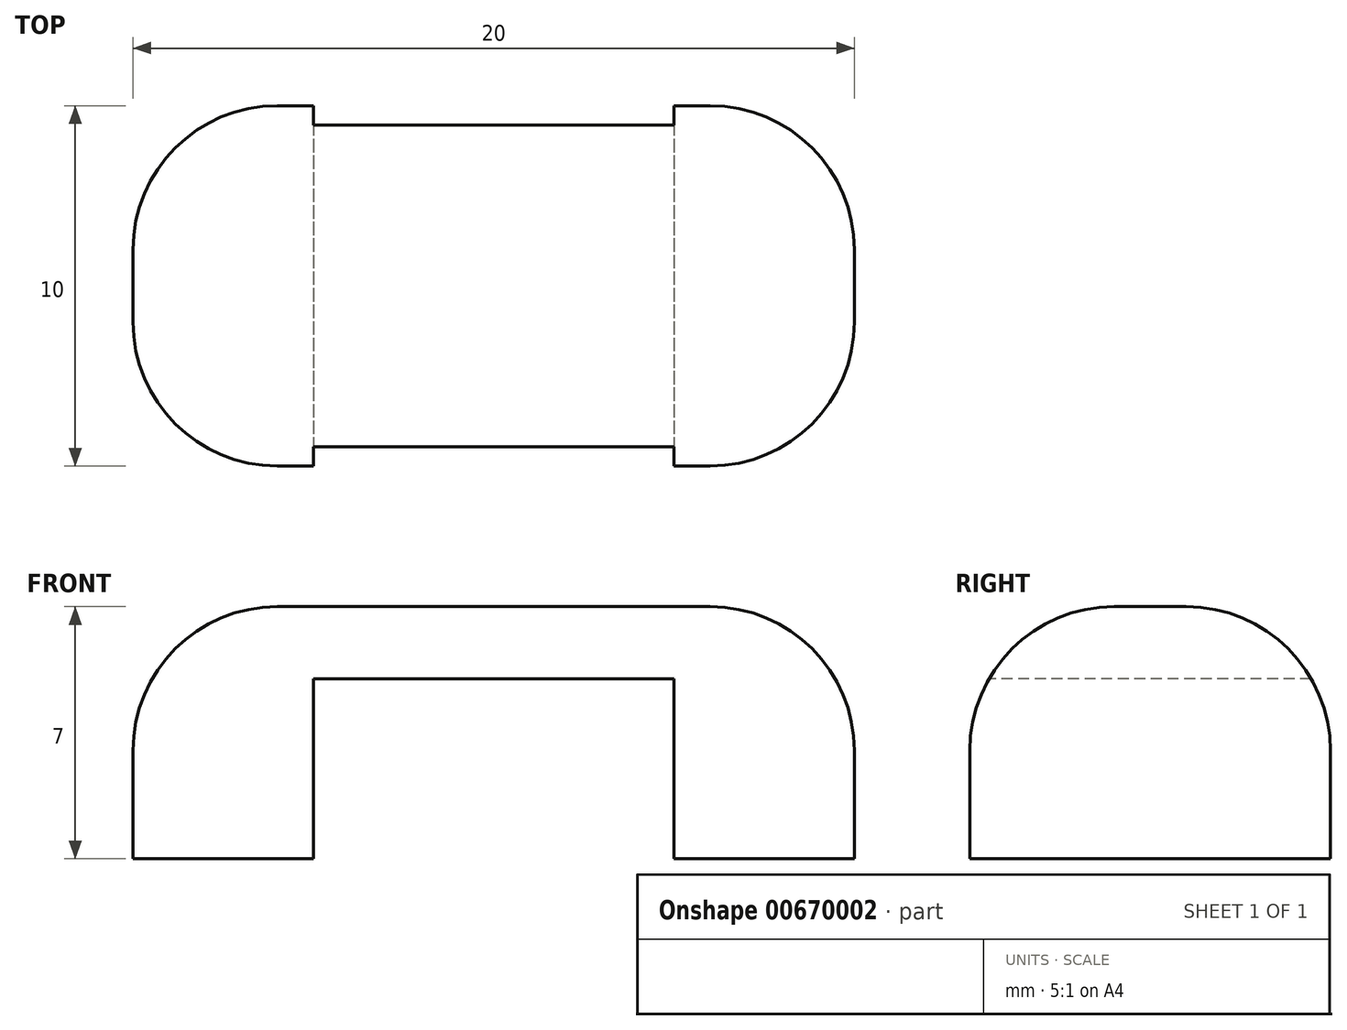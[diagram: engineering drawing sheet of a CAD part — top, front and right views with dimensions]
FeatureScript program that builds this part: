
annotation { "Feature Type Name" : "Feature", "Feature Type Description" : "" }
export const myFeature = defineFeature(function(context is Context, id is Id, definition is map)
    precondition{}
    {
        {
            var Q0;
            Q0=qCreatedBy(makeId("Top.planeOp"),FACE);
            var sketch = newSketch(context, id + "F0", { "sketchPlane" : qUnion([Q0])});
            skLineSegment(sketch, "E0.bottom", {"start": v(-10, 5) * mm, "end": v(-5, 5) * mm});
            skLineSegment(sketch, "E0.top", {"start": v(-10, -5) * mm, "end": v(-5, -5) * mm});
            skLineSegment(sketch, "E0.left", {"start": v(-10, 5) * mm, "end": v(-10, -5) * mm});
            skLineSegment(sketch, "E0.right", {"start": v(-5, 5) * mm, "end": v(-5, -5) * mm});
            skLineSegment(sketch, "E1.bottom", {"start": v(5, 5) * mm, "end": v(10, 5) * mm});
            skLineSegment(sketch, "E1.top", {"start": v(5, -5) * mm, "end": v(10, -5) * mm});
            skLineSegment(sketch, "E1.left", {"start": v(5, 5) * mm, "end": v(5, -5) * mm});
            skLineSegment(sketch, "E1.right", {"start": v(10, 5) * mm, "end": v(10, -5) * mm});
            skSolve(sketch);
        }
        {
            var Q0;
            Q0 = qSketchRegion(id + "F0", true);
            extrude(context, id + "F1", {"entities" : qUnion([Q0]), "depth" : 5 * mm, "offsetDistance" : 25 * mm});
        }
        {
            var Q0;
            Q0=makeQuery(id+"F1.opExtrude","CAP_FACE",FACE,{"disambiguationData":[OSD([sQuery(id+"F0.wireOp",EDGE,"E0.bottom"),sQuery(id+"F0.wireOp",EDGE,"E0.top"),sQuery(id+"F0.wireOp",EDGE,"E0.left"),sQuery(id+"F0.wireOp",EDGE,"E0.right")])],"isStart":false});
            var sketch = newSketch(context, id + "F2", { "sketchPlane" : qUnion([Q0])});
            skLineSegment(sketch, "E2.bottom", {"start": v(-10, -5) * mm, "end": v(10, -5) * mm});
            skLineSegment(sketch, "E2.top", {"start": v(-10, 5) * mm, "end": v(10, 5) * mm});
            skLineSegment(sketch, "E2.left", {"start": v(-10, -5) * mm, "end": v(-10, 5) * mm});
            skLineSegment(sketch, "E2.right", {"start": v(10, -5) * mm, "end": v(10, 5) * mm});
            skSolve(sketch);
        }
        {
            var Q0;
            Q0 = qSketchRegion(id + "F2", true);
            extrude(context, id + "F3", {"entities" : qUnion([Q0]), "operationType" : NewBodyOperationType.ADD, "depth" : 2 * mm, "offsetDistance" : 25 * mm});
        }
        {
            var Q0;
            Q0=makeQuery(id+"F3.opExtrude","CAP_FACE",FACE,{"disambiguationData":[OSD([sQuery(id+"F2.wireOp",EDGE,"E2.bottom"),sQuery(id+"F2.wireOp",EDGE,"E2.top"),sQuery(id+"F2.wireOp",EDGE,"E2.left"),sQuery(id+"F2.wireOp",EDGE,"E2.right")])],"isStart":false});
            var Q1;
            Q1=makeQuery(id+"F3.boolean.opBoolean","MERGE",EDGE,{"derivedFrom":[makeQuery(id+"F1.opExtrude","SWEPT_EDGE",EDGE,{"disambiguationData":[OSD([sQuery(id+"F0.wireOp",EDGE,"E1.top"),sQuery(id+"F0.wireOp",EDGE,"E1.right")])]}),makeQuery(id+"F3.opExtrude","SWEPT_EDGE",EDGE,{"disambiguationData":[OSD([sQuery(id+"F2.wireOp",EDGE,"E2.bottom"),sQuery(id+"F2.wireOp",EDGE,"E2.right")])]})]});
            var Q2;
            Q2=makeQuery(id+"F3.boolean.opBoolean","MERGE",EDGE,{"derivedFrom":[makeQuery(id+"F1.opExtrude","SWEPT_EDGE",EDGE,{"disambiguationData":[OSD([sQuery(id+"F0.wireOp",EDGE,"E1.bottom"),sQuery(id+"F0.wireOp",EDGE,"E1.right")])]}),makeQuery(id+"F3.opExtrude","SWEPT_EDGE",EDGE,{"disambiguationData":[OSD([sQuery(id+"F2.wireOp",EDGE,"E2.top"),sQuery(id+"F2.wireOp",EDGE,"E2.right")])]})]});
            var Q3;
            Q3=makeQuery(id+"F3.boolean.opBoolean","MERGE",EDGE,{"derivedFrom":[makeQuery(id+"F1.opExtrude","SWEPT_EDGE",EDGE,{"disambiguationData":[OSD([sQuery(id+"F0.wireOp",EDGE,"E0.bottom"),sQuery(id+"F0.wireOp",EDGE,"E0.left")])]}),makeQuery(id+"F3.opExtrude","SWEPT_EDGE",EDGE,{"disambiguationData":[OSD([sQuery(id+"F2.wireOp",EDGE,"E2.top"),sQuery(id+"F2.wireOp",EDGE,"E2.left")])]})]});
            var Q4;
            Q4=makeQuery(id+"F3.boolean.opBoolean","MERGE",EDGE,{"derivedFrom":[makeQuery(id+"F1.opExtrude","SWEPT_EDGE",EDGE,{"disambiguationData":[OSD([sQuery(id+"F0.wireOp",EDGE,"E0.top"),sQuery(id+"F0.wireOp",EDGE,"E0.left")])]}),makeQuery(id+"F3.opExtrude","SWEPT_EDGE",EDGE,{"disambiguationData":[OSD([sQuery(id+"F2.wireOp",EDGE,"E2.bottom"),sQuery(id+"F2.wireOp",EDGE,"E2.left")])]})]});
            fillet(context, id + "F4", {"entities" : qUnion([Q0, Q1, Q2, Q3, Q4]), "radius" : 4 * mm, "tangentPropagation" : true, "allowEdgeOverflow" : false});
        }
    });
